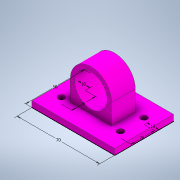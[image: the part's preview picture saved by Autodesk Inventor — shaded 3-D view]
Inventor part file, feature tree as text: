
AUTODESK INVENTOR PART (.ipt)
format: ipt  version: 2022 (Build 260153000, 153)  size: 140,288 bytes
history: native  units: mm
features: sketch x2, extrude x2, hole x1
ambient origin geometry x8: Origin, YZ Plane, XZ Plane, XY Plane, X Axis, Y Axis, Z Axis, Center Point
bodies: Solid1 (feature_tree)
feature tree (5):
  sketch  "Sketch1"  dims[d0=70.0mm d1=50.0mm]
  extrude  "Extrusion1"  Depth=50.0mm
  extrude  "Extrusion2"  Depth=35.0mm
  hole  "Hole2"  [1 undecoded]
  sketch  "Sketch3"  dims[d2=5.0mm d3=0.0mm d13=35.0mm d14=27.5mm d15=20.0mm d16=0.0mm d17=20.0mm d18=20.0mm d19=10.0mm d20=10.0mm d21=5.4mm d22=6.0mm d23=6.0mm d24=2.0mm d25=90.0deg d26=8.0mm d27=20.594885mm]
note: 1 required parameter value undecoded (feature->parameter linkage not recoverable at this tier; creation-order binding heuristic only, values carry confidence <= 0.55)
